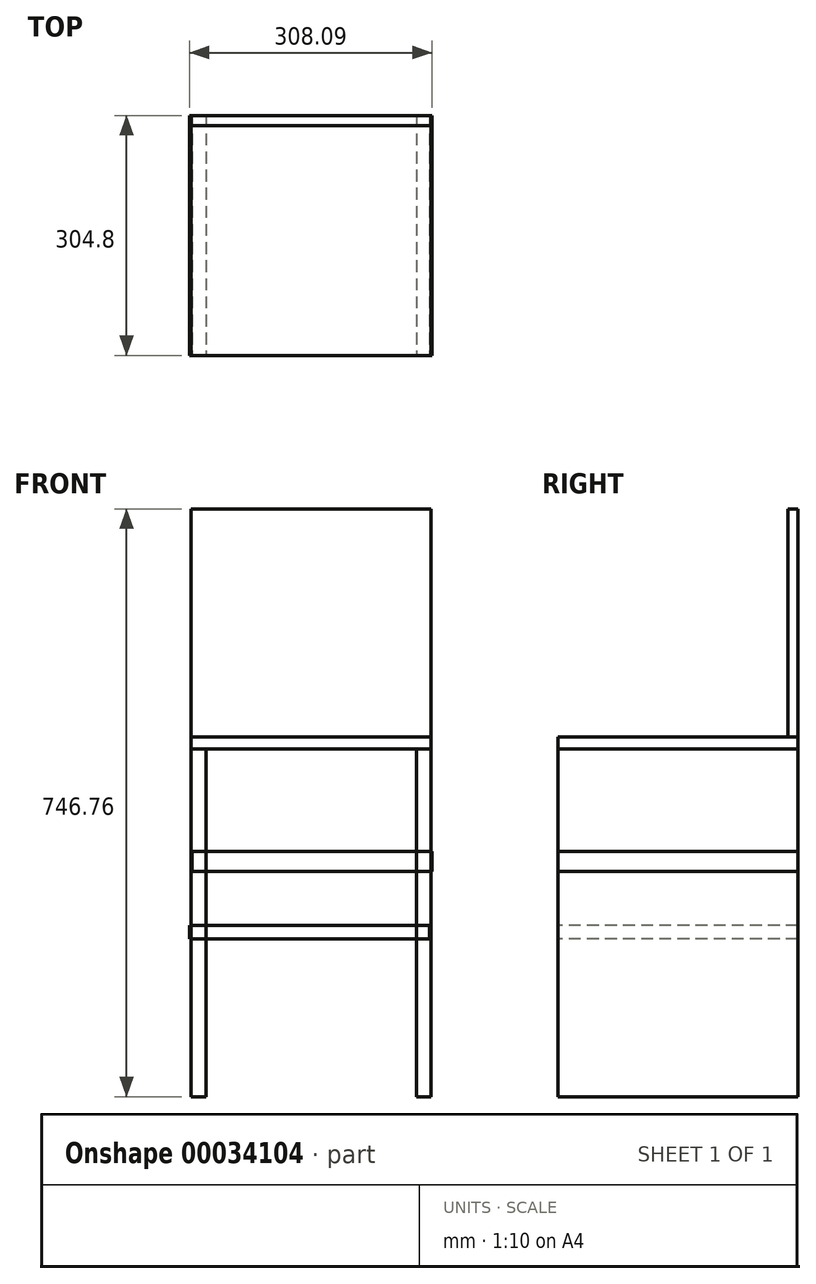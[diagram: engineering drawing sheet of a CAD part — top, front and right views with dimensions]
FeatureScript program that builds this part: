
annotation { "Feature Type Name" : "Feature", "Feature Type Description" : "" }
export const myFeature = defineFeature(function(context is Context, id is Id, definition is map)
    precondition{}
    {
        {
            var Q0;
            Q0=qCreatedBy(makeId("Top.planeOp"),FACE);
            var sketch = newSketch(context, id + "F0", { "sketchPlane" : qUnion([Q0])});
            skLineSegment(sketch, "E0.rect.bottom", {"start": v(-152.4, 152.4) * mm, "end": v(152.4, 152.4) * mm});
            skLineSegment(sketch, "E0.rect.top", {"start": v(-152.4, -152.4) * mm, "end": v(152.4, -152.4) * mm});
            skLineSegment(sketch, "E0.rect.left", {"start": v(-152.4, 152.4) * mm, "end": v(-152.4, -152.4) * mm});
            skLineSegment(sketch, "E0.rect.right", {"start": v(152.4, 152.4) * mm, "end": v(152.4, -152.4) * mm});
            skPoint(sketch, "E0.rect.middle", {"position": v(0, 0) * mm});
            skSolve(sketch);
        }
        {
            var Q0;
            Q0=makeQuery(id+"F0.imprint","IMPRINT",FACE,{"disambiguationData":[TD([[makeQuery(id+"F0.imprint","IMPRINT",EDGE,{"derivedFrom":sQuery(id+"F0.wireOp",EDGE,"E0.rect.bottom")}),-1.0]])]});
            extrude(context, id + "F1", {"entities" : qUnion([Q0]), "depth" : 15.24 * mm});
        }
        {
            var Q0;
            Q0=makeQuery(id+"F1.opExtrude","SWEPT_FACE",FACE,{"disambiguationData":[OSD([sQuery(id+"F0.wireOp",EDGE,"E0.rect.top")])]});
            var sketch = newSketch(context, id + "F2", { "sketchPlane" : qUnion([Q0])});
            skLineSegment(sketch, "E1.bottom", {"start": v(-152.4, 15.24) * mm, "end": v(-133.67, 15.24) * mm});
            skLineSegment(sketch, "E1.top", {"start": v(-152.4, -441.96) * mm, "end": v(-133.67, -441.96) * mm});
            skLineSegment(sketch, "E1.left", {"start": v(-152.4, 15.24) * mm, "end": v(-152.4, -441.96) * mm});
            skLineSegment(sketch, "E1.right", {"start": v(-133.67, 15.24) * mm, "end": v(-133.67, -441.96) * mm});
            skLineSegment(sketch, "E2", {"start": v(0, 18.74) * mm, "end": v(0, -18.32) * mm});
            skLineSegment(sketch, "E3.MirrorCS", {"start": v(133.67, 15.24) * mm, "end": v(133.67, -441.96) * mm});
            skLineSegment(sketch, "E4.MirrorCS", {"start": v(152.4, -441.96) * mm, "end": v(133.67, -441.96) * mm});
            skLineSegment(sketch, "E5.MirrorCS", {"start": v(152.4, 15.24) * mm, "end": v(152.4, -441.96) * mm});
            skLineSegment(sketch, "E6.MirrorCS", {"start": v(152.4, 15.24) * mm, "end": v(133.67, 15.24) * mm});
            skSolve(sketch);
        }
        {
            var Q0;
            {var subQ5=sQuery(id+"F2.wireOp",EDGE,"E1.top");Q0=makeQuery(id+"F2.imprint","IMPRINT",FACE,{"disambiguationData":[TD([[makeQuery(id+"F2.imprint","IMPRINT",EDGE,{"derivedFrom":subQ5}),1.0]])]});}
            var Q1;
            {var subQ5=sQuery(id+"F2.wireOp",EDGE,"E4.MirrorCS");Q1=makeQuery(id+"F2.imprint","IMPRINT",FACE,{"disambiguationData":[TD([[makeQuery(id+"F2.imprint","IMPRINT",EDGE,{"derivedFrom":subQ5}),-1.0]])]});}
            extrude(context, id + "F3", {"entities" : qUnion([Q0, Q1]), "oppositeDirection" : true, "depth" : 304.8 * mm});
        }
        {
            var Q0;
            Q0=makeQuery(id+"F1.opExtrude","SWEPT_FACE",FACE,{"disambiguationData":[OSD([sQuery(id+"F0.wireOp",EDGE,"E0.rect.bottom")])]});
            var sketch = newSketch(context, id + "F4", { "sketchPlane" : qUnion([Q0])});
            skLineSegment(sketch, "E7.bottom", {"start": v(-152.4, 0) * mm, "end": v(152.4, 0) * mm});
            skLineSegment(sketch, "E7.top", {"start": v(-152.4, 304.8) * mm, "end": v(152.4, 304.8) * mm});
            skLineSegment(sketch, "E7.left", {"start": v(-152.4, 0) * mm, "end": v(-152.4, 304.8) * mm});
            skLineSegment(sketch, "E7.right", {"start": v(152.4, 0) * mm, "end": v(152.4, 304.8) * mm});
            skSolve(sketch);
        }
        {
            var Q0;
            {var subQ2=sQuery(id+"F4.wireOp",EDGE,"E7.top");Q0=makeQuery(id+"F4.imprint","IMPRINT",FACE,{"disambiguationData":[TD([[makeQuery(id+"F4.imprint","IMPRINT",EDGE,{"derivedFrom":subQ2}),-1.0]])]});}
            extrude(context, id + "F5", {"entities" : qUnion([Q0]), "oppositeDirection" : true, "depth" : 12.7 * mm});
        }
        {
            var Q0;
            Q0=makeQuery(id+"F1.opExtrude","SWEPT_FACE",FACE,{"disambiguationData":[OSD([sQuery(id+"F0.wireOp",EDGE,"E0.rect.top")])]});
            var sketch = newSketch(context, id + "F6", { "sketchPlane" : qUnion([Q0])});
            skLineSegment(sketch, "E8.bottom", {"start": v(-154.6, -241.6) * mm, "end": v(150.2, -241.6) * mm});
            skLineSegment(sketch, "E8.top", {"start": v(-154.6, -224.1) * mm, "end": v(150.2, -224.1) * mm});
            skLineSegment(sketch, "E8.left", {"start": v(-154.6, -241.6) * mm, "end": v(-154.6, -224.1) * mm});
            skLineSegment(sketch, "E8.right", {"start": v(150.2, -241.6) * mm, "end": v(150.2, -224.1) * mm});
            skSolve(sketch);
        }
        {
            var Q0;
            Q0=makeQuery(id+"F6.imprint","IMPRINT",FACE,{"disambiguationData":[TD([[makeQuery(id+"F6.imprint","IMPRINT",EDGE,{"derivedFrom":sQuery(id+"F6.wireOp",EDGE,"E8.bottom")}),1.0]])]});
            extrude(context, id + "F7", {"entities" : qUnion([Q0]), "oppositeDirection" : true, "depth" : 304.8 * mm});
        }
        {
            var Q0;
            Q0=makeQuery(id+"F1.opExtrude","SWEPT_FACE",FACE,{"disambiguationData":[OSD([sQuery(id+"F0.wireOp",EDGE,"E0.rect.top")])]});
            var sketch = newSketch(context, id + "F8", { "sketchPlane" : qUnion([Q0])});
            skLineSegment(sketch, "E9.bottom", {"start": v(153.5, -155.6) * mm, "end": v(-151.3, -155.6) * mm});
            skLineSegment(sketch, "E9.top", {"start": v(153.5, -130.2) * mm, "end": v(-151.3, -130.2) * mm});
            skLineSegment(sketch, "E9.left", {"start": v(153.5, -155.6) * mm, "end": v(153.5, -130.2) * mm});
            skLineSegment(sketch, "E9.right", {"start": v(-151.3, -155.6) * mm, "end": v(-151.3, -130.2) * mm});
            skSolve(sketch);
        }
        {
            var Q0;
            Q0=makeQuery(id+"F8.imprint","IMPRINT",FACE,{"disambiguationData":[TD([[makeQuery(id+"F8.imprint","IMPRINT",EDGE,{"derivedFrom":sQuery(id+"F8.wireOp",EDGE,"E9.bottom")}),-1.0]])]});
            extrude(context, id + "F9", {"entities" : qUnion([Q0]), "oppositeDirection" : true, "depth" : 304.8 * mm});
        }
    });
